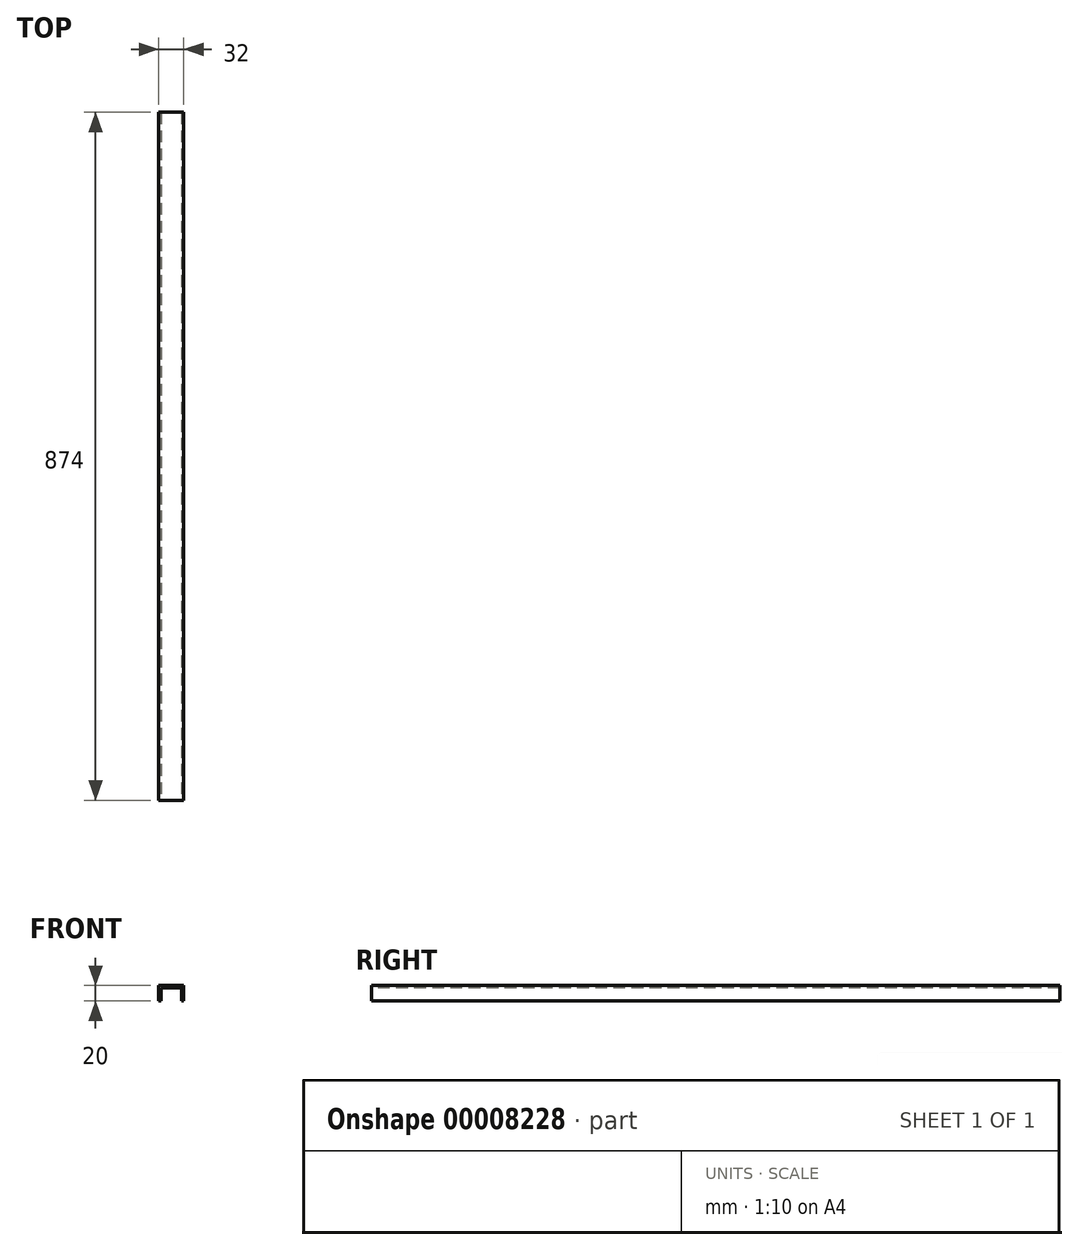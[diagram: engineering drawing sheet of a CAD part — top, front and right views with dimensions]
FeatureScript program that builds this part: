
annotation { "Feature Type Name" : "Feature", "Feature Type Description" : "" }
export const myFeature = defineFeature(function(context is Context, id is Id, definition is map)
    precondition{}
    {
        {
            var Q0;
            Q0=qCreatedBy(makeId("Front.planeOp"),FACE);
            var sketch = newSketch(context, id + "F0", { "sketchPlane" : qUnion([Q0])});
            skLineSegment(sketch, "E0", {"start": v(32, 8.83) * mm, "end": v(32, 28.83) * mm});
            skLineSegment(sketch, "E1", {"start": v(32, 28.83) * mm, "end": v(0, 28.83) * mm});
            skLineSegment(sketch, "E2", {"start": v(0, 28.83) * mm, "end": v(0, 8.83) * mm});
            skLineSegment(sketch, "E3", {"start": v(0, 8.83) * mm, "end": v(3, 8.83) * mm});
            skLineSegment(sketch, "E4", {"start": v(3, 8.83) * mm, "end": v(3, 25.83) * mm});
            skLineSegment(sketch, "E5", {"start": v(3, 25.83) * mm, "end": v(29, 25.83) * mm});
            skLineSegment(sketch, "E6", {"start": v(29, 25.83) * mm, "end": v(29, 8.83) * mm});
            skLineSegment(sketch, "E7", {"start": v(29, 8.83) * mm, "end": v(32, 8.83) * mm});
            skSolve(sketch);
        }
        {
            var Q0;
            Q0=makeQuery(id+"F0.imprint","IMPRINT",FACE,{"disambiguationData":[TD([[makeQuery(id+"F0.imprint","IMPRINT",EDGE,{"derivedFrom":sQuery(id+"F0.wireOp",EDGE,"E0")}),1.0]])]});
            extrude(context, id + "F1", {"entities" : qUnion([Q0]), "oppositeDirection" : true, "depth" : 874 * mm});
        }
    });
